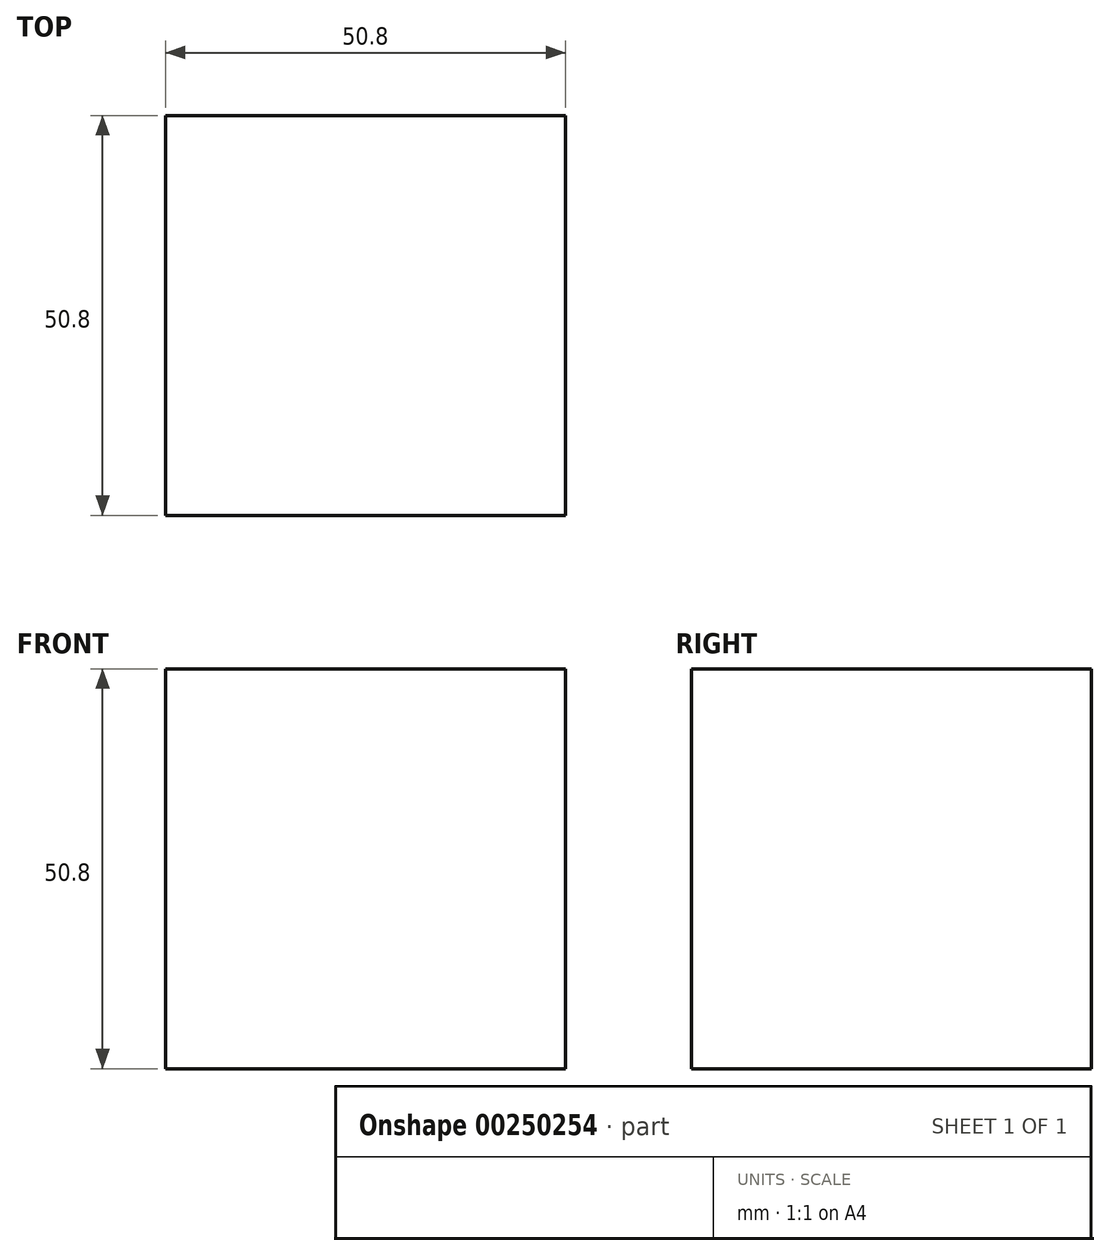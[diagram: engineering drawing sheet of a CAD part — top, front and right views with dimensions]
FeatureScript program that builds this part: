
annotation { "Feature Type Name" : "Feature", "Feature Type Description" : "" }
export const myFeature = defineFeature(function(context is Context, id is Id, definition is map)
    precondition{}
    {
        {
            var Q0;
            Q0=qCreatedBy(makeId("Front.planeOp"),FACE);
            var sketch = newSketch(context, id + "F0", { "sketchPlane" : qUnion([Q0])});
            skLineSegment(sketch, "E0.bottom", {"start": v(-25.4, 25.4) * mm, "end": v(25.4, 25.4) * mm});
            skLineSegment(sketch, "E0.top", {"start": v(-25.4, -25.4) * mm, "end": v(25.4, -25.4) * mm});
            skLineSegment(sketch, "E0.left", {"start": v(-25.4, 25.4) * mm, "end": v(-25.4, -25.4) * mm});
            skLineSegment(sketch, "E0.right", {"start": v(25.4, 25.4) * mm, "end": v(25.4, -25.4) * mm});
            skPoint(sketch, "E0.middle", {"position": v(0, 0) * mm});
            skSolve(sketch);
        }
        {
            var Q0;
            Q0 = qSketchRegion(id + "F0", true);
            extrude(context, id + "F1", {"entities" : qUnion([Q0]), "endBound" : BoundingType.SYMMETRIC, "depth" : 50.8 * mm});
        }
    });
